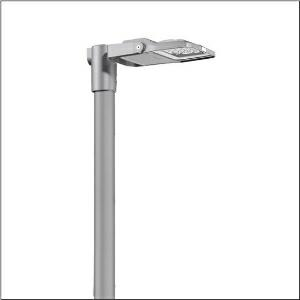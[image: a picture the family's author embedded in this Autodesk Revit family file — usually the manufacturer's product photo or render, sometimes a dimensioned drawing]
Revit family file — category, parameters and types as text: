
# Revit family: floodlight_fl_21_iq_micro___pl33t_5xa7762a2f3a_98d7
name_source: partatom
category: Lighting Fixtures
units: mm (PartAtom-declared; Revit-internal decimal feet)

## family parameters
Cut with Voids When Loaded = No
Host = Face
Light Source = No
Part Type = Normal
Room Calculation Point = No
Round Connector Dimension = Use Diameter
Shared = No

## types (1)
- --- (1 x LED, 2930 lm, 23.1 W, 3000K)
    Apparent Load = 23 VA
    CIE Flux Codes = 26 75 99 100 100
    Color Rendering = 70
    Color Temperature = 3000K
    Default Elevation = 1800 mm
    Description = Floodlight FL 21 iQ micro, floodlight, primary light control with lens, of PMMA, primary optical cover: protective disc, of toughened safety glass, transparent, light distribution: PL33T, light emission: direct distribution, installation type: surface-mounted, LED, High Power LED, rated luminous flux: 2.930lm, luminous efficacy: 127lm/W, light colour: 730, colour temperature: 3000K, control gear: iQ Street-Remote/DALI, control: Auto-Match, Temp-Guard, Night-Set, Smart-Wire, Desk-Remote (wireless, voltage-free reading and setting of iQ features in the workshop via application-optimized NFC function/RFID function), optimised constant luminous flux control (CLO 2.0), Street-Remote, with terminal, 6-pole, mains connection: 220..240V, AC, 50/60Hz, start of lifetime: 23W, end of service life: 24W, reduction: 11W, luminaire housing, of diecast aluminium, powder-coated, Siteco® metallic grey (DB 702S), corrosivity category C5 mid according to DIN EN ISO 12944, suitable for swimming pools, chlorine-resistant, sealing non-destructively replaceable, please order mast flange separately, mast bracket, of steel, galvanised, powder-coated, Siteco® metallic grey (DB 702S), protection rating (complete): IP66, insulation class (complete): insulation class II (safety insulation), certification: CE, ENEC, VDE, protection symbol: D, impact resistance: IK07, permissible operating ambient temperature: -40..+40°C, permissible operating ambient temperature for outdoor applications: -40..+50°C, standard: DIN EN 12944, LABS conformity tested according to VDMA 24364:2018-05, packaging unit: 1 piece

Light Distribution: PL33T
    Height = 65 mm
    Lamp = 1 x LED
    Lamp Light Flux = 2930 lm
    Lamp Power = 23.1 W
    Lamp count = 1
    Length = 312 mm
    Luminous efficacy = 127 lm/W
    Manufacturer = Siteco
    ModVariant = No
    Model = 5XA7762A2F3A
    Number of Poles = 1
    OnlyDefault = Yes
    Power Factor = 1
    Product Name = Floodlight FL 21 iQ micro | PL33T
    Product group = floodlight | pylon annexe
    ProductGroupID = 6200
    Protection Class = Protection class II
    Protection Degree = IP 66
    RLX_Detail_Level = 1
    RLX_Emergency_Light_Flux = 0 lm
    RLX_Emergency_Type = 0
    RLX_Emergency_Type_DB = No
    RlxData = <blob elided: 101729 chars, md5=a146d29c>
    Socket = socket
    Standby Power = 0 W
    System Light Flux = 2930 lm
    System Power = 23 W
    Type Comments = factory setting: luminous flux: 100 % | dim-lin: 254 | 455 mA
    Type Image = l_1007121.jpg
    URL = http://relux.com
    VarID = @adj_147974
    Voltage = 0 V
    Weight = 0.00 kg
    Width = 230 mm

## geometry (parser evidence)
native form markers: Blend x4, Sweep x13
no freeform markers — native parametric forms only
